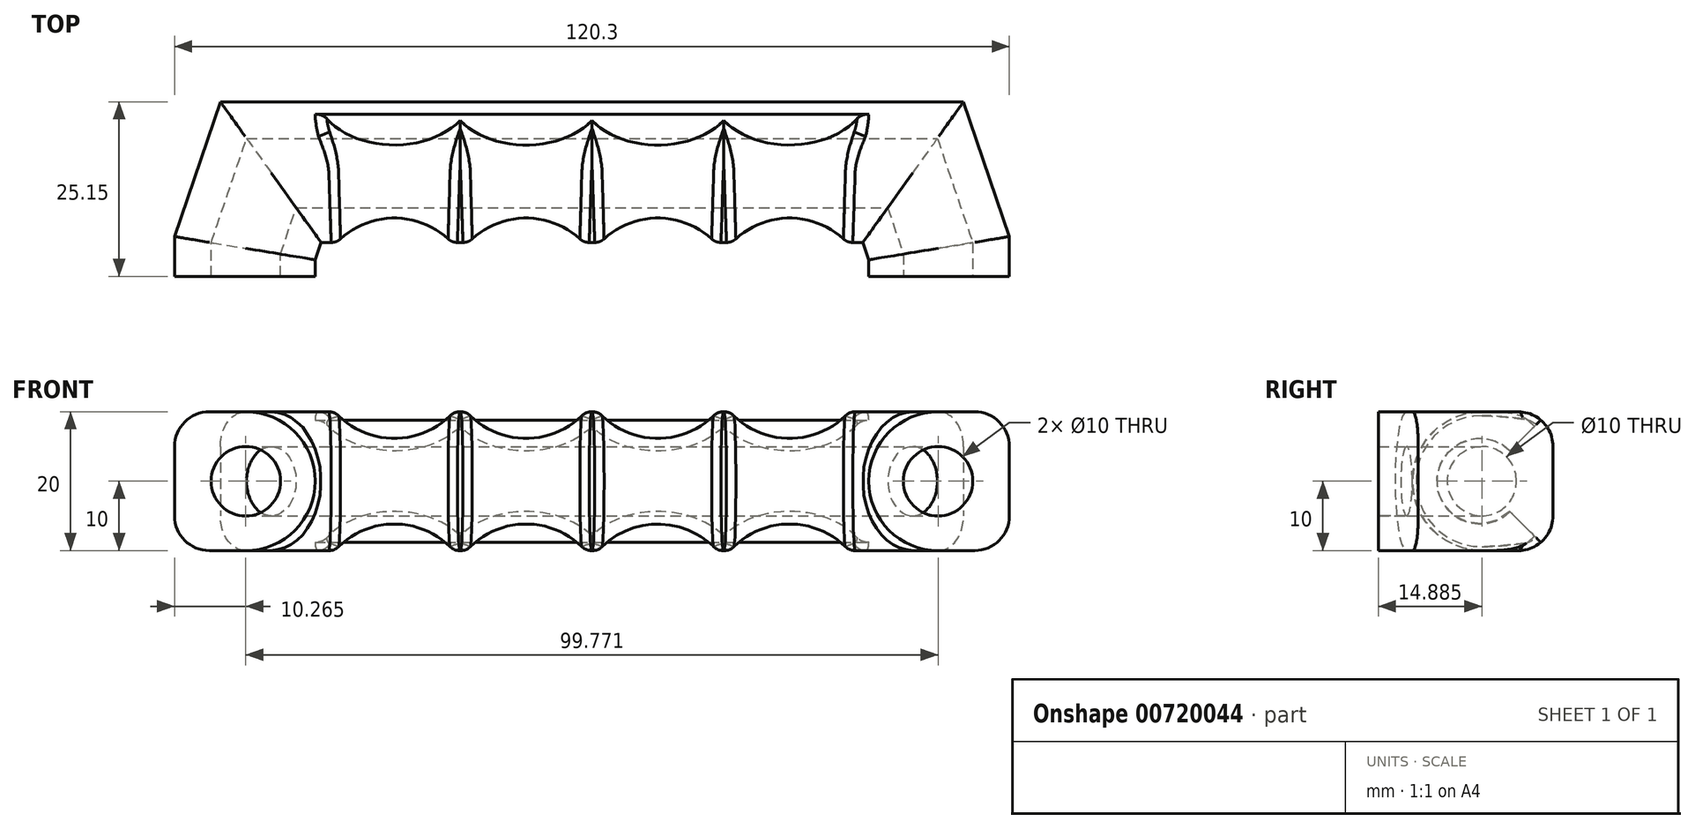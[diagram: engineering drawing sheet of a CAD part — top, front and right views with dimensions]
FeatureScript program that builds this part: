
annotation { "Feature Type Name" : "Feature", "Feature Type Description" : "" }
export const myFeature = defineFeature(function(context is Context, id is Id, definition is map)
    precondition{}
    {
        {
            var Q0;
            Q0=qCreatedBy(makeId("Top.planeOp"),FACE);
            var sketch = newSketch(context, id + "F0", { "sketchPlane" : qUnion([Q0])});
            skLineSegment(sketch, "E0", {"start": v(-35, 14.57) * mm, "end": v(35, 14.57) * mm});
            skLineSegment(sketch, "E1", {"start": v(-35, 0) * mm, "end": v(-35, 14.57) * mm, "construction": true});
            skLineSegment(sketch, "E2", {"start": v(35, 0) * mm, "end": v(35, 14.57) * mm, "construction": true});
            skLineSegment(sketch, "E3", {"start": v(-49.57, 0) * mm, "end": v(-35, 0) * mm, "construction": true});
            skLineSegment(sketch, "E4", {"start": v(-49.57, 0) * mm, "end": v(-49.57, 4) * mm});
            skLineSegment(sketch, "E5", {"start": v(-49.57, 4) * mm, "end": v(-45.98, 14.57) * mm});
            skLineSegment(sketch, "E6", {"start": v(-45.98, 14.57) * mm, "end": v(-35, 14.57) * mm});
            skLineSegment(sketch, "E7.MirrorCS", {"start": v(45.98, 14.57) * mm, "end": v(35, 14.57) * mm});
            skLineSegment(sketch, "E8.MirrorCS", {"start": v(49.57, 4) * mm, "end": v(45.98, 14.57) * mm});
            skLineSegment(sketch, "E9.MirrorCS", {"start": v(49.57, 0) * mm, "end": v(49.57, 4) * mm});
            skSolve(sketch);
        }
        {
            var Q0;
            Q0=qCreatedBy(makeId("Front.planeOp"),FACE);
            var sketch = newSketch(context, id + "F1", { "sketchPlane" : qUnion([Q0])});
            skCircle(sketch, "E10", {"center": v(-49.89, 0) * mm, "radius": 5 * mm});
            skArc(sketch, "E11", {"start": v(-49.89, 10) * mm, "mid": v(-39.89, 0) * mm, "end": v(-49.89, -10) * mm});
            skLineSegment(sketch, "E12", {"start": v(-49.89, -10) * mm, "end": v(-60.15, -10) * mm});
            skLineSegment(sketch, "E13", {"start": v(-60.15, -10) * mm, "end": v(-60.15, 10) * mm});
            skLineSegment(sketch, "E14", {"start": v(-60.15, 10) * mm, "end": v(-49.89, 10) * mm});
            skSolve(sketch);
        }
        {
            var Q0;
            Q0=makeQuery(id+"F1.imprint","IMPRINT",FACE,{"disambiguationData":[TD([[makeQuery(id+"F1.imprint","IMPRINT",EDGE,{"derivedFrom":sQuery(id+"F1.wireOp",EDGE,"E10")}),-1.0]])]});
            var Q1;
            Q1=sQuery(id+"F0.wireOp",EDGE,"E4");
            var Q2;
            Q2=sQuery(id+"F0.wireOp",EDGE,"E5");
            var Q3;
            Q3=sQuery(id+"F0.wireOp",EDGE,"E6");
            var Q4;
            Q4=sQuery(id+"F0.wireOp",EDGE,"E0");
            var Q5;
            Q5=sQuery(id+"F0.wireOp",EDGE,"E7.MirrorCS");
            var Q6;
            Q6=sQuery(id+"F0.wireOp",EDGE,"E8.MirrorCS");
            var Q7;
            Q7=sQuery(id+"F0.wireOp",EDGE,"E9.MirrorCS");
            sweep(context, id + "F2", {"profiles" : qUnion([Q0]), "path" : qUnion([Q1, Q2, Q3, Q4, Q5, Q6, Q7])});
        }
        {
            var Q0;
            Q0=qCreatedBy(makeId("Top.planeOp"),FACE);
            var sketch = newSketch(context, id + "F3", { "sketchPlane" : qUnion([Q0])});
            skCircle(sketch, "E15", {"center": v(-28.48, -3.1) * mm, "radius": 11.5 * mm});
            skCircle(sketch, "E16", {"center": v(-9.5, -3.1) * mm, "radius": 11.5 * mm});
            skCircle(sketch, "E17", {"center": v(9.5, -3.1) * mm, "radius": 11.5 * mm});
            skCircle(sketch, "E18", {"center": v(28.48, -3.1) * mm, "radius": 11.5 * mm});
            skLineSegment(sketch, "E19", {"start": v(-28.48, -3.1) * mm, "end": v(-9.5, -3.1) * mm, "construction": true});
            skLineSegment(sketch, "E20", {"start": v(-9.5, -3.1) * mm, "end": v(9.5, -3.1) * mm, "construction": true});
            skLineSegment(sketch, "E21", {"start": v(9.5, -3.1) * mm, "end": v(28.48, -3.1) * mm, "construction": true});
            skSolve(sketch);
        }
        {
            var Q0;
            {var subQ0=sQuery(id+"F3.wireOp",EDGE,"E16");var subQ1=sQuery(id+"F3.wireOp",EDGE,"E15");var subQ2=makeQuery(id+"F3.imprint","INTERSECT",VERTEX,{"disambiguationData":[OD(0.0)],"derivedFrom":[subQ1,subQ0]});Q0=makeQuery(id+"F3.imprint","IMPRINT",FACE,{"disambiguationData":[TD([[makeQuery(id+"F3.imprint","IMPRINT",EDGE,{"disambiguationData":[TD([[subQ2,-1.0]])],"derivedFrom":subQ1}),1.0]])]});}
            var Q1;
            {var subQ0=sQuery(id+"F3.wireOp",EDGE,"E16");var subQ1=sQuery(id+"F3.wireOp",EDGE,"E15");var subQ2=makeQuery(id+"F3.imprint","INTERSECT",VERTEX,{"disambiguationData":[OD(0.0)],"derivedFrom":[subQ1,subQ0]});Q1=makeQuery(id+"F3.imprint","IMPRINT",FACE,{"disambiguationData":[TD([[makeQuery(id+"F3.imprint","IMPRINT",EDGE,{"disambiguationData":[TD([[subQ2,1.0]])],"derivedFrom":subQ1}),-1.0]])]});}
            var Q2;
            {var subQ0=sQuery(id+"F3.wireOp",EDGE,"E17");var subQ1=sQuery(id+"F3.wireOp",EDGE,"E16");var subQ2=makeQuery(id+"F3.imprint","INTERSECT",VERTEX,{"disambiguationData":[OD(0.0)],"derivedFrom":[subQ1,subQ0]});Q2=makeQuery(id+"F3.imprint","IMPRINT",FACE,{"disambiguationData":[TD([[makeQuery(id+"F3.imprint","IMPRINT",EDGE,{"disambiguationData":[TD([[subQ2,1.0]])],"derivedFrom":subQ1}),-1.0]])]});}
            var Q3;
            {var subQ0=sQuery(id+"F3.wireOp",EDGE,"E18");var subQ1=sQuery(id+"F3.wireOp",EDGE,"E17");var subQ2=makeQuery(id+"F3.imprint","INTERSECT",VERTEX,{"disambiguationData":[OD(0.0)],"derivedFrom":[subQ1,subQ0]});Q3=makeQuery(id+"F3.imprint","IMPRINT",FACE,{"disambiguationData":[TD([[makeQuery(id+"F3.imprint","IMPRINT",EDGE,{"disambiguationData":[TD([[subQ2,1.0]])],"derivedFrom":subQ1}),-1.0]])]});}
            var Q4;
            {var subQ0=sQuery(id+"F3.wireOp",EDGE,"E16");var subQ1=sQuery(id+"F3.wireOp",EDGE,"E15");var subQ2=makeQuery(id+"F3.imprint","INTERSECT",VERTEX,{"disambiguationData":[OD(0.0)],"derivedFrom":[subQ1,subQ0]});Q4=makeQuery(id+"F3.imprint","IMPRINT",FACE,{"disambiguationData":[TD([[makeQuery(id+"F3.imprint","IMPRINT",EDGE,{"disambiguationData":[TD([[subQ2,1.0]])],"derivedFrom":subQ1}),1.0]])]});}
            var Q5;
            {var subQ0=sQuery(id+"F3.wireOp",EDGE,"E17");var subQ1=sQuery(id+"F3.wireOp",EDGE,"E16");var subQ2=makeQuery(id+"F3.imprint","INTERSECT",VERTEX,{"disambiguationData":[OD(0.0)],"derivedFrom":[subQ1,subQ0]});Q5=makeQuery(id+"F3.imprint","IMPRINT",FACE,{"disambiguationData":[TD([[makeQuery(id+"F3.imprint","IMPRINT",EDGE,{"disambiguationData":[TD([[subQ2,1.0]])],"derivedFrom":subQ1}),1.0]])]});}
            var Q6;
            {var subQ0=sQuery(id+"F3.wireOp",EDGE,"E18");var subQ1=sQuery(id+"F3.wireOp",EDGE,"E17");var subQ2=makeQuery(id+"F3.imprint","INTERSECT",VERTEX,{"disambiguationData":[OD(0.0)],"derivedFrom":[subQ1,subQ0]});Q6=makeQuery(id+"F3.imprint","IMPRINT",FACE,{"disambiguationData":[TD([[makeQuery(id+"F3.imprint","IMPRINT",EDGE,{"disambiguationData":[TD([[subQ2,1.0]])],"derivedFrom":subQ1}),1.0]])]});}
            var Q7;
            Q7=sQuery(id+"F0.wireOp",EDGE,"E0");
            revolve(context, id + "F4", {"operationType" : NewBodyOperationType.REMOVE, "surfaceOperationType" : NewSurfaceOperationType.NEW, "entities" : qUnion([Q0, Q1, Q2, Q3, Q4, Q5, Q6]), "axis" : qUnion([Q7]), "revolveType" : RevolveType.SYMMETRIC, "oppositeDirection" : true, "angle" : 270 * degree});
        }
        {
            var Q0;
            Q0=makeQuery(id+"F2.opSweep","SWEPT_EDGE",EDGE,{"disambiguationData":[OSD([sQuery(id+"F0.wireOp",EDGE,"WraTuVpF-8g27-8P2T-GBwI-SE2XuV1BzHSC"),sQuery(id+"F1.wireOp",EDGE,"E13"),sQuery(id+"F1.wireOp",EDGE,"E14")])]});
            var Q1;
            Q1=makeQuery(id+"F2.opSweep","SWEPT_EDGE",EDGE,{"disambiguationData":[OSD([sQuery(id+"F0.wireOp",EDGE,"E0"),sQuery(id+"F1.wireOp",EDGE,"E13"),sQuery(id+"F1.wireOp",EDGE,"E14")])]});
            var Q2;
            Q2=makeQuery(id+"F2.opSweep","SWEPT_EDGE",EDGE,{"disambiguationData":[OSD([sQuery(id+"F0.wireOp",EDGE,"c0afe523-84ed-4378-855d-37e15938762f0.MirrorCS"),sQuery(id+"F1.wireOp",EDGE,"E13"),sQuery(id+"F1.wireOp",EDGE,"E14")])]});
            var Q3;
            Q3=makeQuery(id+"F2.opSweep","SWEPT_EDGE",EDGE,{"disambiguationData":[OSD([sQuery(id+"F0.wireOp",EDGE,"WraTuVpF-8g27-8P2T-GBwI-SE2XuV1BzHSC"),sQuery(id+"F1.wireOp",EDGE,"E12"),sQuery(id+"F1.wireOp",EDGE,"E13")])]});
            var Q4;
            Q4=makeQuery(id+"F2.opSweep","SWEPT_EDGE",EDGE,{"disambiguationData":[OSD([sQuery(id+"F0.wireOp",EDGE,"c0afe523-84ed-4378-855d-37e15938762f0.MirrorCS"),sQuery(id+"F1.wireOp",EDGE,"E12"),sQuery(id+"F1.wireOp",EDGE,"E13")])]});
            fillet(context, id + "F5", {"entities" : qUnion([Q0, Q1, Q2, Q3, Q4]), "radius" : 5 * mm, "tangentPropagation" : true, "allowEdgeOverflow" : false});
        }
        {
            var Q0;
            Q0=makeQuery(id+"F4.boolean.opBoolean","INTERSECT",EDGE,{"disambiguationData":[OD(1.0)],"derivedFrom":[makeQuery(id+"F2.opSweep","SWEPT_FACE",FACE,{"disambiguationData":[OSD([sQuery(id+"F0.wireOp",EDGE,"E7.MirrorCS"),sQuery(id+"F1.wireOp",EDGE,"E11")])]}),makeQuery(id+"F4.opRevolve","SWEPT_FACE",FACE,{"disambiguationData":[OSD([sQuery(id+"F3.wireOp",EDGE,"E15")])]})]});
            var Q1;
            {var subQ0=sQuery(id+"F3.wireOp",EDGE,"E16");Q1=makeQuery(id+"F4.boolean.opBoolean","INTERSECT",EDGE,{"disambiguationData":[OD(0.0)],"derivedFrom":[makeQuery(id+"F2.opSweep","SWEPT_FACE",FACE,{"disambiguationData":[OSD([sQuery(id+"F0.wireOp",EDGE,"E7.MirrorCS"),sQuery(id+"F1.wireOp",EDGE,"E11")])]}),makeQuery(id+"F4.opRevolve","SWEPT_FACE",FACE,{"disambiguationData":[OSD([subQ0]),TDD([makeQuery(id+"F3.imprint","IMPRINT",EDGE,{"disambiguationData":[TD([[makeQuery(id+"F3.imprint","INTERSECT",VERTEX,{"disambiguationData":[OD(0.0)],"derivedFrom":[sQuery(id+"F3.wireOp",EDGE,"E15"),subQ0]}),1.0]])],"derivedFrom":subQ0})])]})]});}
            var Q2;
            {var subQ0=sQuery(id+"F3.wireOp",EDGE,"E16");Q2=makeQuery(id+"F4.boolean.opBoolean","INTERSECT",EDGE,{"disambiguationData":[OD(1.0)],"derivedFrom":[makeQuery(id+"F2.opSweep","SWEPT_FACE",FACE,{"disambiguationData":[OSD([sQuery(id+"F0.wireOp",EDGE,"E7.MirrorCS"),sQuery(id+"F1.wireOp",EDGE,"E11")])]}),makeQuery(id+"F4.opRevolve","SWEPT_FACE",FACE,{"disambiguationData":[OSD([subQ0]),TDD([makeQuery(id+"F3.imprint","IMPRINT",EDGE,{"disambiguationData":[TD([[makeQuery(id+"F3.imprint","INTERSECT",VERTEX,{"disambiguationData":[OD(0.0)],"derivedFrom":[sQuery(id+"F3.wireOp",EDGE,"E15"),subQ0]}),1.0]])],"derivedFrom":subQ0})])]})]});}
            var Q3;
            {var subQ0=sQuery(id+"F3.wireOp",EDGE,"E17");Q3=makeQuery(id+"F4.boolean.opBoolean","INTERSECT",EDGE,{"disambiguationData":[OD(0.0)],"derivedFrom":[makeQuery(id+"F2.opSweep","SWEPT_FACE",FACE,{"disambiguationData":[OSD([sQuery(id+"F0.wireOp",EDGE,"E7.MirrorCS"),sQuery(id+"F1.wireOp",EDGE,"E11")])]}),makeQuery(id+"F4.opRevolve","SWEPT_FACE",FACE,{"disambiguationData":[OSD([subQ0]),TDD([makeQuery(id+"F3.imprint","IMPRINT",EDGE,{"disambiguationData":[TD([[makeQuery(id+"F3.imprint","INTERSECT",VERTEX,{"disambiguationData":[OD(0.0)],"derivedFrom":[sQuery(id+"F3.wireOp",EDGE,"E16"),subQ0]}),1.0]])],"derivedFrom":subQ0})])]})]});}
            var Q4;
            {var subQ0=sQuery(id+"F3.wireOp",EDGE,"E17");Q4=makeQuery(id+"F4.boolean.opBoolean","INTERSECT",EDGE,{"disambiguationData":[OD(1.0)],"derivedFrom":[makeQuery(id+"F2.opSweep","SWEPT_FACE",FACE,{"disambiguationData":[OSD([sQuery(id+"F0.wireOp",EDGE,"E7.MirrorCS"),sQuery(id+"F1.wireOp",EDGE,"E11")])]}),makeQuery(id+"F4.opRevolve","SWEPT_FACE",FACE,{"disambiguationData":[OSD([subQ0]),TDD([makeQuery(id+"F3.imprint","IMPRINT",EDGE,{"disambiguationData":[TD([[makeQuery(id+"F3.imprint","INTERSECT",VERTEX,{"disambiguationData":[OD(0.0)],"derivedFrom":[sQuery(id+"F3.wireOp",EDGE,"E16"),subQ0]}),1.0]])],"derivedFrom":subQ0})])]})]});}
            var Q5;
            Q5=makeQuery(id+"F4.boolean.opBoolean","INTERSECT",EDGE,{"disambiguationData":[OD(1.0)],"derivedFrom":[makeQuery(id+"F2.opSweep","SWEPT_FACE",FACE,{"disambiguationData":[OSD([sQuery(id+"F0.wireOp",EDGE,"E7.MirrorCS"),sQuery(id+"F1.wireOp",EDGE,"E11")])]}),makeQuery(id+"F4.opRevolve","SWEPT_FACE",FACE,{"disambiguationData":[OSD([sQuery(id+"F3.wireOp",EDGE,"E18")])]})]});
            var Q6;
            Q6=makeQuery(id+"F4.boolean.opBoolean","INTERSECT",EDGE,{"disambiguationData":[OD(0.0)],"derivedFrom":[makeQuery(id+"F2.opSweep","SWEPT_FACE",FACE,{"disambiguationData":[OSD([sQuery(id+"F0.wireOp",EDGE,"E7.MirrorCS"),sQuery(id+"F1.wireOp",EDGE,"E11")])]}),makeQuery(id+"F4.opRevolve","SWEPT_FACE",FACE,{"disambiguationData":[OSD([sQuery(id+"F3.wireOp",EDGE,"E15")])]})]});
            var Q7;
            Q7=makeQuery(id+"F4.boolean.opBoolean","INTERSECT",EDGE,{"disambiguationData":[OD(0.0)],"derivedFrom":[makeQuery(id+"F2.opSweep","SWEPT_FACE",FACE,{"disambiguationData":[OSD([sQuery(id+"F0.wireOp",EDGE,"E7.MirrorCS"),sQuery(id+"F1.wireOp",EDGE,"E11")])]}),makeQuery(id+"F4.opRevolve","SWEPT_FACE",FACE,{"disambiguationData":[OSD([sQuery(id+"F3.wireOp",EDGE,"E18")])]})]});
            fillet(context, id + "F6", {"entities" : qUnion([Q0, Q1, Q2, Q3, Q4, Q5, Q6, Q7]), "radius" : 2 * mm, "tangentPropagation" : true, "allowEdgeOverflow" : false});
        }
    });
